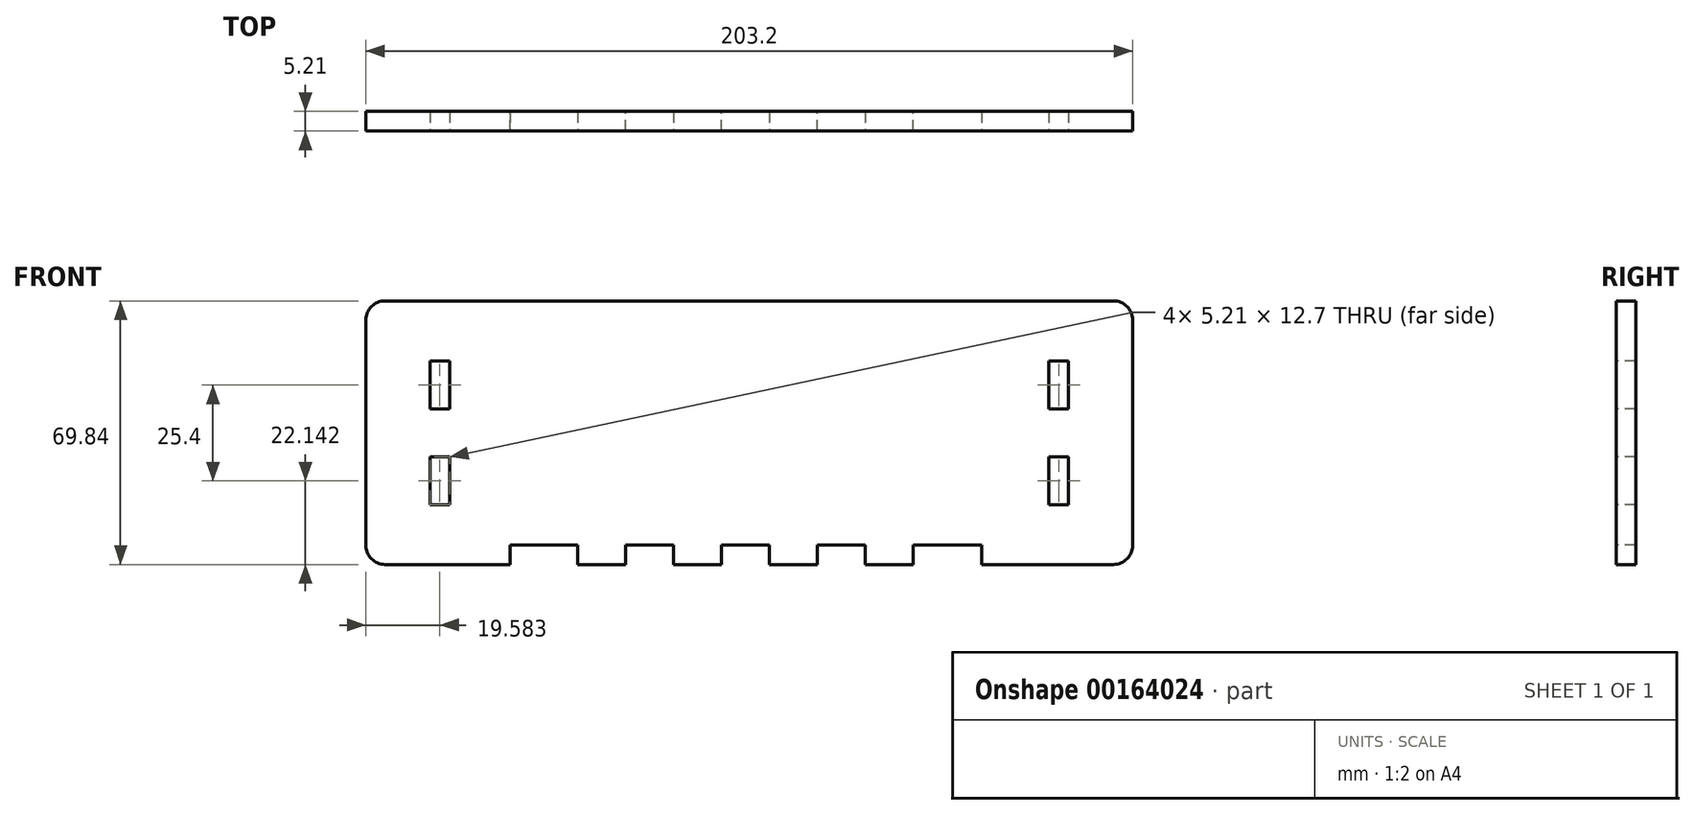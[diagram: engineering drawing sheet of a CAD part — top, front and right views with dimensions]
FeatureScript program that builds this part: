
annotation { "Feature Type Name" : "Feature", "Feature Type Description" : "" }
export const myFeature = defineFeature(function(context is Context, id is Id, definition is map)
    precondition{}
    {
        {
            var Q0;
            Q0=qCreatedBy(makeId("Front.planeOp"),FACE);
            var sketch = newSketch(context, id + "F0", { "sketchPlane" : qUnion([Q0])});
            skLineSegment(sketch, "E0.bottom", {"start": v(101.6, -34.93) * mm, "end": v(-101.6, -34.93) * mm});
            skLineSegment(sketch, "E0.top", {"start": v(101.6, 34.93) * mm, "end": v(-101.6, 34.92) * mm});
            skLineSegment(sketch, "E0.left", {"start": v(101.6, -34.93) * mm, "end": v(101.6, 34.93) * mm});
            skLineSegment(sketch, "E0.right", {"start": v(-101.6, -34.93) * mm, "end": v(-101.6, 34.92) * mm});
            skPoint(sketch, "E0.middle", {"position": v(0, 0) * mm});
            skSolve(sketch);
        }
        {
            var Q0;
            Q0=makeQuery(id+"F0.imprint","IMPRINT",FACE,{"disambiguationData":[TD([[makeQuery(id+"F0.imprint","IMPRINT",EDGE,{"derivedFrom":sQuery(id+"F0.wireOp",EDGE,"E0.bottom")}),-1.0]])]});
            extrude(context, id + "F1", {"entities" : qUnion([Q0]), "depth" : 5.2 * mm});
        }
        {
            var Q0;
            Q0=makeQuery(id+"F1.opExtrude","SWEPT_EDGE",EDGE,{"disambiguationData":[OSD([sQuery(id+"F0.wireOp",EDGE,"E0.top"),sQuery(id+"F0.wireOp",EDGE,"E0.right")])]});
            var Q1;
            Q1=makeQuery(id+"F1.opExtrude","SWEPT_EDGE",EDGE,{"disambiguationData":[OSD([sQuery(id+"F0.wireOp",EDGE,"E0.bottom"),sQuery(id+"F0.wireOp",EDGE,"E0.right")])]});
            var Q2;
            Q2=makeQuery(id+"F1.opExtrude","SWEPT_EDGE",EDGE,{"disambiguationData":[OSD([sQuery(id+"F0.wireOp",EDGE,"E0.bottom"),sQuery(id+"F0.wireOp",EDGE,"E0.left")])]});
            var Q3;
            Q3=makeQuery(id+"F1.opExtrude","SWEPT_EDGE",EDGE,{"disambiguationData":[OSD([sQuery(id+"F0.wireOp",EDGE,"E0.top"),sQuery(id+"F0.wireOp",EDGE,"E0.left")])]});
            fillet(context, id + "F2", {"entities" : qUnion([Q0, Q1, Q2, Q3]), "radius" : 5.08 * mm, "tangentPropagation" : true, "allowEdgeOverflow" : false});
        }
        {
            var Q0;
            Q0=makeQuery(id+"F1.opExtrude","CAP_FACE",FACE,{"disambiguationData":[OSD([sQuery(id+"F0.wireOp",EDGE,"E0.bottom"),sQuery(id+"F0.wireOp",EDGE,"E0.top"),sQuery(id+"F0.wireOp",EDGE,"E0.left"),sQuery(id+"F0.wireOp",EDGE,"E0.right")])],"isStart":false});
            var sketch = newSketch(context, id + "F3", { "sketchPlane" : qUnion([Q0])});
            skLineSegment(sketch, "E1", {"start": v(61.56, -35) * mm, "end": v(61.56, -29.8) * mm});
            skLineSegment(sketch, "E2", {"start": v(61.56, -29.8) * mm, "end": v(43.46, -29.8) * mm});
            skLineSegment(sketch, "E3", {"start": v(43.46, -29.8) * mm, "end": v(43.46, -35) * mm});
            skLineSegment(sketch, "E4", {"start": v(30.76, -35) * mm, "end": v(30.76, -29.8) * mm});
            skLineSegment(sketch, "E5", {"start": v(30.76, -29.8) * mm, "end": v(18.06, -29.8) * mm});
            skLineSegment(sketch, "E6", {"start": v(18.06, -29.8) * mm, "end": v(18.06, -35) * mm});
            skLineSegment(sketch, "E7", {"start": v(5.36, -35) * mm, "end": v(5.36, -29.8) * mm});
            skLineSegment(sketch, "E8", {"start": v(5.36, -29.8) * mm, "end": v(-7.34, -29.8) * mm});
            skLineSegment(sketch, "E9", {"start": v(-7.34, -29.8) * mm, "end": v(-7.34, -35) * mm});
            skLineSegment(sketch, "E10", {"start": v(-20.04, -35) * mm, "end": v(-20.04, -29.8) * mm});
            skLineSegment(sketch, "E11", {"start": v(-20.04, -29.8) * mm, "end": v(-32.74, -29.8) * mm});
            skLineSegment(sketch, "E12", {"start": v(-32.74, -29.8) * mm, "end": v(-32.74, -35) * mm});
            skLineSegment(sketch, "E13", {"start": v(-45.44, -35) * mm, "end": v(-45.44, -29.8) * mm});
            skLineSegment(sketch, "E14", {"start": v(-45.44, -29.8) * mm, "end": v(-63.4, -29.8) * mm});
            skLineSegment(sketch, "E15", {"start": v(-63.4, -29.8) * mm, "end": v(-63.38, -35) * mm});
            skLineSegment(sketch, "E16", {"start": v(-84.62, -19.13) * mm, "end": v(-79.41, -19.13) * mm});
            skLineSegment(sketch, "E17", {"start": v(-79.41, -19.13) * mm, "end": v(-79.41, -6.43) * mm});
            skLineSegment(sketch, "E18", {"start": v(-79.41, -6.43) * mm, "end": v(-84.62, -6.43) * mm});
            skLineSegment(sketch, "E19", {"start": v(-84.62, 6.27) * mm, "end": v(-79.41, 6.27) * mm});
            skLineSegment(sketch, "E20", {"start": v(-79.41, 6.27) * mm, "end": v(-79.41, 18.97) * mm});
            skLineSegment(sketch, "E21", {"start": v(-79.41, 18.97) * mm, "end": v(-84.62, 18.97) * mm});
            skLineSegment(sketch, "E22", {"start": v(84.62, -19.13) * mm, "end": v(79.41, -19.13) * mm});
            skLineSegment(sketch, "E23", {"start": v(79.41, -19.13) * mm, "end": v(79.41, -6.43) * mm});
            skLineSegment(sketch, "E24", {"start": v(79.41, -6.43) * mm, "end": v(84.62, -6.43) * mm});
            skLineSegment(sketch, "E25", {"start": v(84.62, 6.27) * mm, "end": v(79.41, 6.27) * mm});
            skLineSegment(sketch, "E26", {"start": v(79.41, 6.27) * mm, "end": v(79.41, 18.97) * mm});
            skLineSegment(sketch, "E27", {"start": v(79.41, 18.97) * mm, "end": v(84.62, 18.97) * mm});
            skLineSegment(sketch, "E28", {"start": v(-84.62, 18.97) * mm, "end": v(-84.62, 6.27) * mm});
            skLineSegment(sketch, "E29", {"start": v(-84.62, -6.43) * mm, "end": v(-84.62, -19.13) * mm});
            skLineSegment(sketch, "E30", {"start": v(-63.38, -35) * mm, "end": v(-45.44, -35) * mm});
            skLineSegment(sketch, "E31", {"start": v(-32.74, -35) * mm, "end": v(-20.04, -35) * mm});
            skLineSegment(sketch, "E32", {"start": v(-7.34, -35) * mm, "end": v(5.36, -35) * mm});
            skLineSegment(sketch, "E33", {"start": v(18.06, -35) * mm, "end": v(30.76, -35) * mm});
            skLineSegment(sketch, "E34", {"start": v(43.46, -35) * mm, "end": v(61.56, -35) * mm});
            skLineSegment(sketch, "E35", {"start": v(84.62, -19.13) * mm, "end": v(84.62, -6.43) * mm});
            skLineSegment(sketch, "E36", {"start": v(84.62, 18.97) * mm, "end": v(84.62, 6.27) * mm});
            skSolve(sketch);
        }
        {
            var Q0;
            Q0=makeQuery(id+"F3.imprint","IMPRINT",FACE,{"disambiguationData":[TD([[makeQuery(id+"F3.imprint","IMPRINT",EDGE,{"derivedFrom":sQuery(id+"F3.wireOp",EDGE,"E19")}),1.0]])]});
            var Q1;
            Q1=makeQuery(id+"F3.imprint","IMPRINT",FACE,{"disambiguationData":[TD([[makeQuery(id+"F3.imprint","IMPRINT",EDGE,{"derivedFrom":sQuery(id+"F3.wireOp",EDGE,"E16")}),1.0]])]});
            var Q2;
            Q2=makeQuery(id+"F3.imprint","IMPRINT",FACE,{"disambiguationData":[TD([[makeQuery(id+"F3.imprint","IMPRINT",EDGE,{"derivedFrom":sQuery(id+"F3.wireOp",EDGE,"E13")}),1.0]])]});
            var Q3;
            Q3=makeQuery(id+"F3.imprint","IMPRINT",FACE,{"disambiguationData":[TD([[makeQuery(id+"F3.imprint","IMPRINT",EDGE,{"derivedFrom":sQuery(id+"F3.wireOp",EDGE,"E10")}),1.0]])]});
            var Q4;
            Q4=makeQuery(id+"F3.imprint","IMPRINT",FACE,{"disambiguationData":[TD([[makeQuery(id+"F3.imprint","IMPRINT",EDGE,{"derivedFrom":sQuery(id+"F3.wireOp",EDGE,"E7")}),1.0]])]});
            var Q5;
            Q5=makeQuery(id+"F3.imprint","IMPRINT",FACE,{"disambiguationData":[TD([[makeQuery(id+"F3.imprint","IMPRINT",EDGE,{"derivedFrom":sQuery(id+"F3.wireOp",EDGE,"E4")}),1.0]])]});
            var Q6;
            Q6=makeQuery(id+"F3.imprint","IMPRINT",FACE,{"disambiguationData":[TD([[makeQuery(id+"F3.imprint","IMPRINT",EDGE,{"derivedFrom":sQuery(id+"F3.wireOp",EDGE,"E1")}),1.0]])]});
            var Q7;
            Q7=makeQuery(id+"F3.imprint","IMPRINT",FACE,{"disambiguationData":[TD([[makeQuery(id+"F3.imprint","IMPRINT",EDGE,{"derivedFrom":sQuery(id+"F3.wireOp",EDGE,"E22")}),-1.0]])]});
            var Q8;
            Q8=makeQuery(id+"F3.imprint","IMPRINT",FACE,{"disambiguationData":[TD([[makeQuery(id+"F3.imprint","IMPRINT",EDGE,{"derivedFrom":sQuery(id+"F3.wireOp",EDGE,"E25")}),-1.0]])]});
            extrude(context, id + "F4", {"entities" : qUnion([Q0, Q1, Q2, Q3, Q4, Q5, Q6, Q7, Q8]), "operationType" : NewBodyOperationType.REMOVE, "endBound" : BoundingType.THROUGH_ALL, "oppositeDirection" : true, "depth" : 25.4 * mm});
        }
    });
